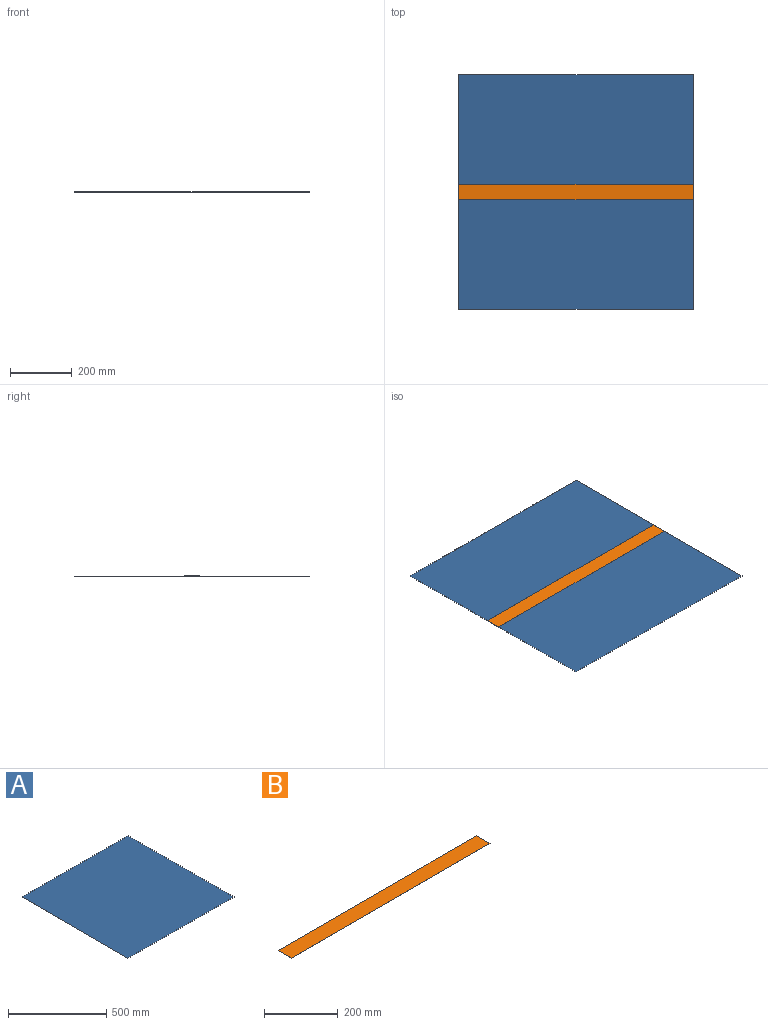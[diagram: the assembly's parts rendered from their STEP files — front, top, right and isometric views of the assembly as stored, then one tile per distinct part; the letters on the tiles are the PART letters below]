
ASSEMBLY  parts=2 mates=1
PART A: 6 faces, bbox 762x762x0.3 mm
  f0: plane 762x0.25mm, normal (0,1,0), area 193.5mm2, adj f1,f3,f4,f5
  f1: plane 762x0.25mm, normal (-1,0,0), area 193.5mm2, adj f0,f2,f4,f5
  f2: plane 762x0.25mm, normal (0,-1,0), area 193.5mm2, adj f1,f3,f4,f5
  f3: plane 762x0.25mm, normal (1,0,0), area 193.5mm2, adj f0,f2,f4,f5
  f4: plane 762x762mm, normal (0,0,1), area 580644mm2, adj f0,f1,f2,f3
  f5: plane 762x762mm, normal (0,0,-1), area 580644mm2, adj f0,f1,f2,f3
PART B: 6 faces, bbox 762x50.8x0.3 mm
  f0: plane 50.8x0.25mm, normal (-1,0,0), area 12.9mm2, adj f1,f3,f4,f5
  f1: plane 762x0.25mm, normal (0,-1,0), area 193.5mm2, adj f0,f2,f4,f5
  f2: plane 50.8x0.25mm, normal (1,0,0), area 12.9mm2, adj f1,f3,f4,f5
  f3: plane 762x0.25mm, normal (0,1,0), area 193.5mm2, adj f0,f2,f4,f5
  f4: plane 762x50.8mm, normal (0,0,1), area 38709.6mm2, adj f0,f1,f2,f3
  f5: plane 762x50.8mm, normal (0,0,-1), area 38709.6mm2, adj f0,f1,f2,f3
PLACE A t=(70.36,-232.92,155.72)mm
PLACE B rot(axis=(1,0,0),180deg) t=(-356.78,82.31,156.22)mm
MATE fastened B.f4 <-> A.f4  axis (0,0,-1) through (-81.39,56.91,155.97)mm
